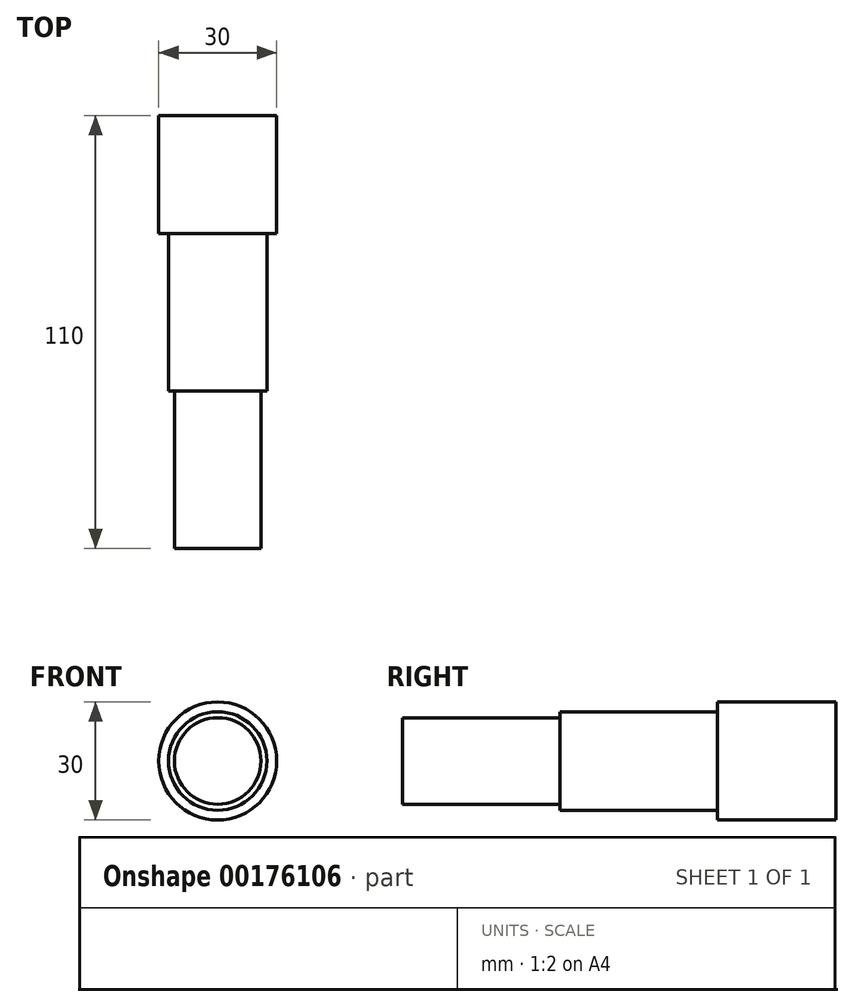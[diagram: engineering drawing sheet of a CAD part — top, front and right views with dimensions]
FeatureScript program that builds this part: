
annotation { "Feature Type Name" : "Feature", "Feature Type Description" : "" }
export const myFeature = defineFeature(function(context is Context, id is Id, definition is map)
    precondition{}
    {
        {
            var Q0;
            Q0=qCreatedBy(makeId("Right.planeOp"),FACE);
            var sketch = newSketch(context, id + "F0", { "sketchPlane" : qUnion([Q0])});
            skLineSegment(sketch, "E0", {"start": v(-110, 0) * mm, "end": v(-110, 11) * mm});
            skLineSegment(sketch, "E1", {"start": v(-110, 11) * mm, "end": v(-70, 11) * mm});
            skLineSegment(sketch, "E2", {"start": v(-70, 11) * mm, "end": v(-70, 12.5) * mm});
            skLineSegment(sketch, "E3", {"start": v(-70, 12.5) * mm, "end": v(-30, 12.5) * mm});
            skLineSegment(sketch, "E4", {"start": v(-30, 12.5) * mm, "end": v(-30, 15) * mm});
            skLineSegment(sketch, "E5", {"start": v(-30, 15) * mm, "end": v(0, 15) * mm});
            skLineSegment(sketch, "E6", {"start": v(0, 15) * mm, "end": v(0, 0) * mm});
            skLineSegment(sketch, "E7", {"start": v(0, 0) * mm, "end": v(-110, 0) * mm});
            skSolve(sketch);
        }
        {
            var Q0;
            Q0 = qSketchRegion(id + "F0", true);
            var Q1;
            Q1=sQuery(id+"F0.wireOp",EDGE,"E7");
            revolve(context, id + "F1", {"entities" : qUnion([Q0]), "axis" : qUnion([Q1]), "revolveType" : RevolveType.FULL});
        }
    });
